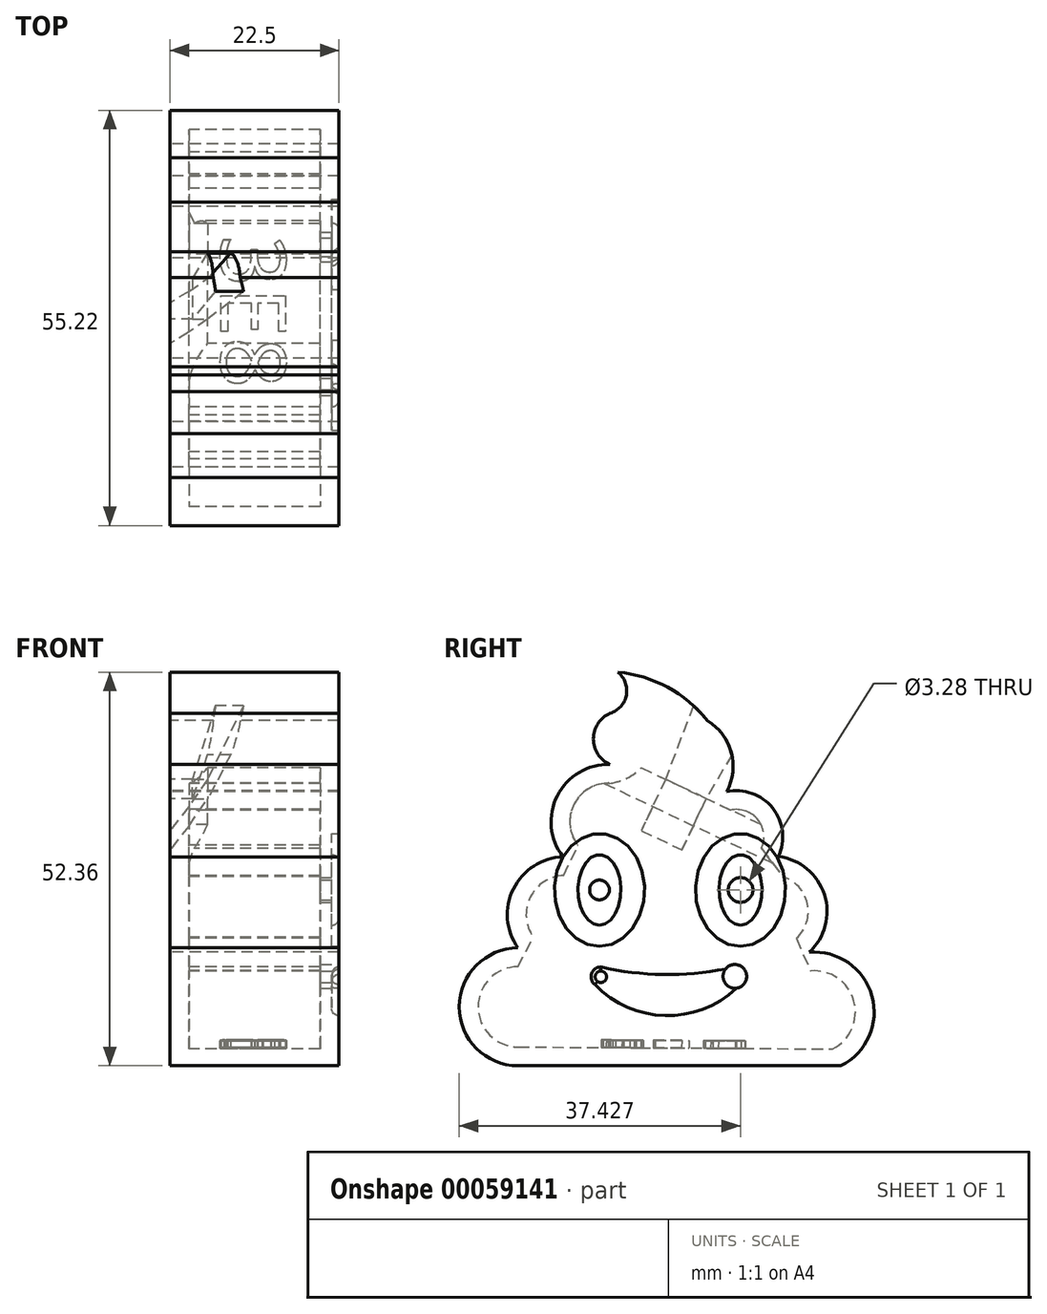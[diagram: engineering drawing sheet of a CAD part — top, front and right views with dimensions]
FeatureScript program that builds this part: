
annotation { "Feature Type Name" : "Feature", "Feature Type Description" : "" }
export const myFeature = defineFeature(function(context is Context, id is Id, definition is map)
    precondition{}
    {
        {
            var Q0;
            Q0=qCreatedBy(makeId("Top.planeOp"),FACE);
            var sketch = newSketch(context, id + "F0", { "sketchPlane" : qUnion([Q0])});
            skArc(sketch, "E0", {"start": v(-7.78, 52.75) * mm, "mid": v(-5.62, 55.18) * mm, "end": v(-6.74, 58.22) * mm});
            skArc(sketch, "E1", {"start": v(-7.78, 52.75) * mm, "mid": v(-10, 49.35) * mm, "end": v(-7.78, 45.95) * mm});
            skArc(sketch, "E2", {"start": v(-7.78, 45.95) * mm, "mid": v(-14.8, 41.8) * mm, "end": v(-14.04, 33.67) * mm});
            skArc(sketch, "E3", {"start": v(-14.04, 33.67) * mm, "mid": v(-20.65, 29.4) * mm, "end": v(-20.05, 21.54) * mm});
            skArc(sketch, "E4", {"start": v(-20.05, 21.54) * mm, "mid": v(-27.84, 13.7) * mm, "end": v(-20.05, 5.86) * mm});
            skArc(sketch, "E5", {"start": v(22.95, 5.86) * mm, "mid": v(27.07, 15.17) * mm, "end": v(18.7, 20.97) * mm});
            skArc(sketch, "E6", {"start": v(18.7, 20.97) * mm, "mid": v(20.75, 28.65) * mm, "end": v(14.63, 33.7) * mm});
            skArc(sketch, "E7", {"start": v(14.63, 33.7) * mm, "mid": v(13.85, 40.15) * mm, "end": v(7.74, 42.32) * mm});
            skArc(sketch, "E8", {"start": v(7.74, 42.32) * mm, "mid": v(8.35, 47.56) * mm, "end": v(5.18, 51.77) * mm});
            skArc(sketch, "E9", {"start": v(5.18, 51.77) * mm, "mid": v(-0.12, 56.22) * mm, "end": v(-6.74, 58.22) * mm});
            skLineSegment(sketch, "E10", {"start": v(-20.05, 5.86) * mm, "end": v(22.95, 5.86) * mm});
            skSolve(sketch);
        }
        {
            var Q0;
            Q0=makeQuery(id+"F0.imprint","IMPRINT",FACE,{"disambiguationData":[TD([[makeQuery(id+"F0.imprint","IMPRINT",EDGE,{"derivedFrom":sQuery(id+"F0.wireOp",EDGE,"E0")}),-1.0]])]});
            extrude(context, id + "F1", {"entities" : qUnion([Q0]), "depth" : 2.5 * mm});
        }
        {
            var Q0;
            Q0=makeQuery(id+"F1.opExtrude","CAP_FACE",FACE,{"disambiguationData":[OSD([sQuery(id+"F0.wireOp",EDGE,"E0"),sQuery(id+"F0.wireOp",EDGE,"E1"),sQuery(id+"F0.wireOp",EDGE,"E2"),sQuery(id+"F0.wireOp",EDGE,"E3"),sQuery(id+"F0.wireOp",EDGE,"E4"),sQuery(id+"F0.wireOp",EDGE,"E5"),sQuery(id+"F0.wireOp",EDGE,"E6"),sQuery(id+"F0.wireOp",EDGE,"E7"),sQuery(id+"F0.wireOp",EDGE,"E8"),sQuery(id+"F0.wireOp",EDGE,"E9"),sQuery(id+"F0.wireOp",EDGE,"E10")])],"isStart":false});
            var sketch = newSketch(context, id + "F2", { "sketchPlane" : qUnion([Q0])});
            skArc(sketch, "E11.0", {"start": v(-7.85, 43.45) * mm, "mid": v(-12.57, 40.66) * mm, "end": v(-12.06, 35.2) * mm});
            skArc(sketch, "E12.0", {"start": v(-13.94, 31.17) * mm, "mid": v(-18.4, 28.28) * mm, "end": v(-18, 22.98) * mm});
            skArc(sketch, "E13.0", {"start": v(-20.04, 19.04) * mm, "mid": v(-25.34, 13.7) * mm, "end": v(-20.04, 8.36) * mm});
            skArc(sketch, "E14.0", {"start": v(21.83, 8.1) * mm, "mid": v(24.67, 14.5) * mm, "end": v(18.92, 18.48) * mm});
            skArc(sketch, "E15.0", {"start": v(17.02, 22.82) * mm, "mid": v(18.48, 27.44) * mm, "end": v(15.22, 31.03) * mm});
            skArc(sketch, "E16.0", {"start": v(12.36, 34.76) * mm, "mid": v(11.9, 38.6) * mm, "end": v(8.27, 39.88) * mm});
            skLineSegment(sketch, "E17", {"start": v(-20.04, 8.36) * mm, "end": v(21.83, 8.1) * mm});
            skArc(sketch, "E18.0", {"start": v(5.18, 51.77) * mm, "mid": v(-0.12, 56.22) * mm, "end": v(-6.74, 58.22) * mm});
            skArc(sketch, "E19.0", {"start": v(7.74, 42.32) * mm, "mid": v(8.35, 47.56) * mm, "end": v(5.18, 51.77) * mm});
            skArc(sketch, "E20.0", {"start": v(14.63, 33.7) * mm, "mid": v(13.85, 40.15) * mm, "end": v(7.74, 42.32) * mm});
            skArc(sketch, "E21.0", {"start": v(18.7, 20.97) * mm, "mid": v(20.75, 28.65) * mm, "end": v(14.63, 33.7) * mm});
            skArc(sketch, "E22.0", {"start": v(22.95, 5.86) * mm, "mid": v(27.07, 15.17) * mm, "end": v(18.7, 20.97) * mm});
            skLineSegment(sketch, "E23.0", {"start": v(-20.05, 5.86) * mm, "end": v(22.95, 5.86) * mm});
            skArc(sketch, "E24.0", {"start": v(-20.05, 21.54) * mm, "mid": v(-27.84, 13.7) * mm, "end": v(-20.05, 5.86) * mm});
            skArc(sketch, "E25.0", {"start": v(-14.04, 33.67) * mm, "mid": v(-20.65, 29.4) * mm, "end": v(-20.05, 21.54) * mm});
            skArc(sketch, "E26.0", {"start": v(-7.78, 45.95) * mm, "mid": v(-14.8, 41.8) * mm, "end": v(-14.04, 33.67) * mm});
            skArc(sketch, "E27.0", {"start": v(-7.78, 52.75) * mm, "mid": v(-10, 49.35) * mm, "end": v(-7.78, 45.95) * mm});
            skArc(sketch, "E28.0", {"start": v(-7.78, 52.75) * mm, "mid": v(-5.62, 55.18) * mm, "end": v(-6.74, 58.22) * mm});
            skLineSegment(sketch, "E29", {"start": v(-20.04, 19.04) * mm, "end": v(-18, 22.98) * mm});
            skLineSegment(sketch, "E30", {"start": v(-13.94, 31.17) * mm, "end": v(-12.06, 35.2) * mm});
            skLineSegment(sketch, "E31", {"start": v(12.36, 34.76) * mm, "end": v(15.22, 31.03) * mm});
            skLineSegment(sketch, "E32", {"start": v(17.02, 22.82) * mm, "end": v(18.92, 18.48) * mm});
            skArc(sketch, "E33", {"start": v(-7.85, 43.45) * mm, "mid": v(-5.56, 44.12) * mm, "end": v(-3.62, 45.51) * mm});
            skLineSegment(sketch, "E34", {"start": v(-3.62, 45.51) * mm, "end": v(8.27, 39.88) * mm});
            skSolve(sketch);
        }
        {
            var Q0;
            Q0 = qSketchRegion(id + "F2", true);
            extrude(context, id + "F3", {"entities" : qUnion([Q0]), "operationType" : NewBodyOperationType.ADD, "depth" : 20 * mm});
        }
        {
            var Q0;
            Q0=makeQuery(id+"F3.opExtrude","SWEPT_FACE",FACE,{"disambiguationData":[OSD([sQuery(id+"F2.wireOp",EDGE,"E34")])]});
            var sketch = newSketch(context, id + "F4", { "sketchPlane" : qUnion([Q0])});
            skLineSegment(sketch, "E35.top", {"start": v(-19.19, 5) * mm, "end": v(-13.19, 5) * mm});
            skLineSegment(sketch, "E35.left", {"start": v(-19.19, 3) * mm, "end": v(-19.19, 5) * mm});
            skLineSegment(sketch, "E35.right", {"start": v(-13.19, 3) * mm, "end": v(-13.19, 5) * mm});
            skPoint(sketch, "E36", {"position": v(-16.19, 2.5) * mm});
            skLineSegment(sketch, "E37", {"start": v(-16.19, 2.5) * mm, "end": v(-16.19, 3) * mm, "construction": true});
            skLineSegment(sketch, "E38", {"start": v(-13.19, 3) * mm, "end": v(-19.19, 3) * mm});
            skSolve(sketch);
        }
        {
            var Q0;
            Q0=makeQuery(id+"F1.opExtrude","CAP_FACE",FACE,{"disambiguationData":[OSD([sQuery(id+"F0.wireOp",EDGE,"E0"),sQuery(id+"F0.wireOp",EDGE,"E1"),sQuery(id+"F0.wireOp",EDGE,"E2"),sQuery(id+"F0.wireOp",EDGE,"E3"),sQuery(id+"F0.wireOp",EDGE,"E4"),sQuery(id+"F0.wireOp",EDGE,"E5"),sQuery(id+"F0.wireOp",EDGE,"E6"),sQuery(id+"F0.wireOp",EDGE,"E7"),sQuery(id+"F0.wireOp",EDGE,"E8"),sQuery(id+"F0.wireOp",EDGE,"E9"),sQuery(id+"F0.wireOp",EDGE,"E10")])],"isStart":true});
            var sketch = newSketch(context, id + "F5", { "sketchPlane" : qUnion([Q0])});
            skLineSegment(sketch, "E39", {"start": v(-0.39, -43.98) * mm, "end": v(-1.46, -41.72) * mm});
            skLineSegment(sketch, "E40", {"start": v(-1.46, -41.72) * mm, "end": v(3.97, -39.15) * mm});
            skLineSegment(sketch, "E41", {"start": v(3.97, -39.15) * mm, "end": v(5.04, -41.4) * mm});
            skLineSegment(sketch, "E42", {"start": v(5.04, -41.4) * mm, "end": v(-0.39, -43.98) * mm});
            skPoint(sketch, "E43", {"position": v(2.33, -42.7) * mm});
            skPoint(sketch, "E44.0", {"position": v(-3.62, -45.51) * mm});
            skPoint(sketch, "E45.0", {"position": v(8.27, -39.88) * mm});
            skLineSegment(sketch, "E46", {"start": v(-3.62, -45.51) * mm, "end": v(8.27, -39.88) * mm, "construction": true});
            skSolve(sketch);
        }
        {
            var Q0;
            Q0=makeQuery(id+"F3.opExtrude","CAP_FACE",FACE,{"disambiguationData":[OSD([sQuery(id+"F2.wireOp",EDGE,"E11.0"),sQuery(id+"F2.wireOp",EDGE,"E12.0"),sQuery(id+"F2.wireOp",EDGE,"E13.0"),sQuery(id+"F2.wireOp",EDGE,"E14.0"),sQuery(id+"F2.wireOp",EDGE,"E15.0"),sQuery(id+"F2.wireOp",EDGE,"E16.0"),sQuery(id+"F2.wireOp",EDGE,"E17"),sQuery(id+"F2.wireOp",EDGE,"E18.0"),sQuery(id+"F2.wireOp",EDGE,"E19.0"),sQuery(id+"F2.wireOp",EDGE,"E20.0"),sQuery(id+"F2.wireOp",EDGE,"E21.0"),sQuery(id+"F2.wireOp",EDGE,"E22.0"),sQuery(id+"F2.wireOp",EDGE,"E23.0"),sQuery(id+"F2.wireOp",EDGE,"E24.0"),sQuery(id+"F2.wireOp",EDGE,"E25.0"),sQuery(id+"F2.wireOp",EDGE,"E26.0"),sQuery(id+"F2.wireOp",EDGE,"E27.0"),sQuery(id+"F2.wireOp",EDGE,"E28.0"),sQuery(id+"F2.wireOp",EDGE,"E29"),sQuery(id+"F2.wireOp",EDGE,"E30"),sQuery(id+"F2.wireOp",EDGE,"E31"),sQuery(id+"F2.wireOp",EDGE,"E32"),sQuery(id+"F2.wireOp",EDGE,"E33"),sQuery(id+"F2.wireOp",EDGE,"E34")])],"isStart":false});
            var sketch = newSketch(context, id + "F6", { "sketchPlane" : qUnion([Q0])});
            skLineSegment(sketch, "E47.0", {"start": v(-3.62, 45.51) * mm, "end": v(8.27, 39.88) * mm});
            skArc(sketch, "E48.0", {"start": v(-7.85, 43.45) * mm, "mid": v(-5.56, 44.12) * mm, "end": v(-3.62, 45.51) * mm});
            skArc(sketch, "E49.0", {"start": v(-7.85, 43.45) * mm, "mid": v(-12.57, 40.66) * mm, "end": v(-12.06, 35.2) * mm});
            skLineSegment(sketch, "E50.0", {"start": v(-13.94, 31.17) * mm, "end": v(-12.06, 35.2) * mm});
            skArc(sketch, "E51.0", {"start": v(-13.94, 31.17) * mm, "mid": v(-18.4, 28.28) * mm, "end": v(-18, 22.98) * mm});
            skLineSegment(sketch, "E52.0", {"start": v(-20.04, 19.04) * mm, "end": v(-18, 22.98) * mm});
            skArc(sketch, "E53.0", {"start": v(-20.04, 19.04) * mm, "mid": v(-25.34, 13.7) * mm, "end": v(-20.04, 8.36) * mm});
            skLineSegment(sketch, "E54.0", {"start": v(-20.04, 8.36) * mm, "end": v(21.83, 8.1) * mm});
            skArc(sketch, "E55.0", {"start": v(21.83, 8.1) * mm, "mid": v(24.67, 14.5) * mm, "end": v(18.92, 18.48) * mm});
            skLineSegment(sketch, "E56.0", {"start": v(17.02, 22.82) * mm, "end": v(18.92, 18.48) * mm});
            skArc(sketch, "E57.0", {"start": v(17.02, 22.82) * mm, "mid": v(18.48, 27.44) * mm, "end": v(15.22, 31.03) * mm});
            skLineSegment(sketch, "E58.0", {"start": v(12.36, 34.76) * mm, "end": v(15.22, 31.03) * mm});
            skArc(sketch, "E59.0", {"start": v(12.36, 34.76) * mm, "mid": v(11.9, 38.6) * mm, "end": v(8.27, 39.88) * mm});
            skSolve(sketch);
        }
        {
            var Q0;
            Q0=makeQuery(id+"F6.imprint","IMPRINT",FACE,{"disambiguationData":[TD([[makeQuery(id+"F6.imprint","IMPRINT",EDGE,{"derivedFrom":sQuery(id+"F6.wireOp",EDGE,"E47.0")}),-1.0]])]});
            extrude(context, id + "F7", {"entities" : qUnion([Q0]), "operationType" : NewBodyOperationType.ADD, "oppositeDirection" : true, "depth" : 2.5 * mm});
        }
        {
            var Q0;
            Q0=makeQuery(id+"F7.boolean.opBoolean","MERGE",FACE,{"derivedFrom":[makeQuery(id+"F3.opExtrude","CAP_FACE",FACE,{"disambiguationData":[OSD([sQuery(id+"F2.wireOp",EDGE,"E11.0"),sQuery(id+"F2.wireOp",EDGE,"E12.0"),sQuery(id+"F2.wireOp",EDGE,"E13.0"),sQuery(id+"F2.wireOp",EDGE,"E14.0"),sQuery(id+"F2.wireOp",EDGE,"E15.0"),sQuery(id+"F2.wireOp",EDGE,"E16.0"),sQuery(id+"F2.wireOp",EDGE,"E17"),sQuery(id+"F2.wireOp",EDGE,"E18.0"),sQuery(id+"F2.wireOp",EDGE,"E19.0"),sQuery(id+"F2.wireOp",EDGE,"E20.0"),sQuery(id+"F2.wireOp",EDGE,"E21.0"),sQuery(id+"F2.wireOp",EDGE,"E22.0"),sQuery(id+"F2.wireOp",EDGE,"E23.0"),sQuery(id+"F2.wireOp",EDGE,"E24.0"),sQuery(id+"F2.wireOp",EDGE,"E25.0"),sQuery(id+"F2.wireOp",EDGE,"E26.0"),sQuery(id+"F2.wireOp",EDGE,"E27.0"),sQuery(id+"F2.wireOp",EDGE,"E28.0"),sQuery(id+"F2.wireOp",EDGE,"E29"),sQuery(id+"F2.wireOp",EDGE,"E30"),sQuery(id+"F2.wireOp",EDGE,"E31"),sQuery(id+"F2.wireOp",EDGE,"E32"),sQuery(id+"F2.wireOp",EDGE,"E33"),sQuery(id+"F2.wireOp",EDGE,"E34")])],"isStart":false}),makeQuery(id+"F7.opExtrude","CAP_FACE",FACE,{"disambiguationData":[OSD([sQuery(id+"F6.wireOp",EDGE,"E47.0"),sQuery(id+"F6.wireOp",EDGE,"E48.0"),sQuery(id+"F6.wireOp",EDGE,"E49.0"),sQuery(id+"F6.wireOp",EDGE,"E50.0"),sQuery(id+"F6.wireOp",EDGE,"E51.0"),sQuery(id+"F6.wireOp",EDGE,"E52.0"),sQuery(id+"F6.wireOp",EDGE,"E53.0"),sQuery(id+"F6.wireOp",EDGE,"E54.0"),sQuery(id+"F6.wireOp",EDGE,"E55.0"),sQuery(id+"F6.wireOp",EDGE,"E56.0"),sQuery(id+"F6.wireOp",EDGE,"E57.0"),sQuery(id+"F6.wireOp",EDGE,"E58.0"),sQuery(id+"F6.wireOp",EDGE,"E59.0")])],"isStart":true})]});
            var sketch = newSketch(context, id + "F8", { "sketchPlane" : qUnion([Q0])});
            skLineSegment(sketch, "E60", {"start": v(1.45, 5.86) * mm, "end": v(0.2, 5.86) * mm, "construction": true});
            skLineSegment(sketch, "E61", {"start": v(0.2, 5.86) * mm, "end": v(0.2, 39.46) * mm, "construction": true});
            skLineSegment(sketch, "E62", {"start": v(0.2, 29.25) * mm, "end": v(-9.18, 29.25) * mm, "construction": true});
            skEllipse(sketch, "E63", {"center": v(-9.18, 29.25) * mm, "majorRadius": 7.5 * mm, "minorRadius": 6 * mm, "majorAxis": v(0, -1)});
            skEllipse(sketch, "E64.MirrorC", {"center": v(9.58, 29.25) * mm, "majorRadius": 7.5 * mm, "minorRadius": 6 * mm, "majorAxis": v(0, -1)});
            skArc(sketch, "E65", {"start": v(-9, 19) * mm, "mid": v(-0.09, 18) * mm, "end": v(8.83, 19) * mm});
            skLineSegment(sketch, "E66", {"start": v(-9, 19) * mm, "end": v(8.83, 19) * mm, "construction": true});
            skArc(sketch, "E67", {"start": v(-9.79, 16.67) * mm, "mid": v(0.02, 12.54) * mm, "end": v(9.73, 16.9) * mm});
            skArc(sketch, "E68", {"start": v(-9, 19) * mm, "mid": v(-10.24, 18.12) * mm, "end": v(-9.79, 16.67) * mm});
            skArc(sketch, "E69", {"start": v(9.73, 16.9) * mm, "mid": v(9.97, 18.25) * mm, "end": v(8.83, 19) * mm});
            skSolve(sketch);
        }
        {
            var Q0;
            Q0 = qSketchRegion(id + "F8", true);
            extrude(context, id + "F9", {"entities" : qUnion([Q0]), "operationType" : NewBodyOperationType.REMOVE, "oppositeDirection" : true, "depth" : 1 * mm});
        }
        {
            var Q0;
            Q0=makeQuery(id+"F9.boolean.opBoolean","COPY",FACE,{"derivedFrom":makeQuery(id+"F9.opExtrude","CAP_FACE",FACE,{"disambiguationData":[OSD([sQuery(id+"F8.wireOp",EDGE,"E63")])],"isStart":false})});
            var sketch = newSketch(context, id + "F10", { "sketchPlane" : qUnion([Q0])});
            skPoint(sketch, "E70.0", {"position": v(-9.18, 29.25) * mm});
            skLineSegment(sketch, "E71.0", {"start": v(0.2, 5.86) * mm, "end": v(0.2, 39.46) * mm, "construction": true});
            skEllipse(sketch, "E72", {"center": v(-9.18, 29.25) * mm, "majorRadius": 4.69 * mm, "minorRadius": 2.86 * mm, "majorAxis": v(0, -1)});
            skEllipse(sketch, "E73.MirrorC", {"center": v(9.58, 29.25) * mm, "majorRadius": 4.69 * mm, "minorRadius": 2.86 * mm, "majorAxis": v(0, -1)});
            skSolve(sketch);
        }
        {
            var Q0;
            Q0 = qSketchRegion(id + "F10", true);
            extrude(context, id + "F11", {"entities" : qUnion([Q0]), "operationType" : NewBodyOperationType.ADD, "depth" : 1 * mm});
        }
        {
            var Q0;
            Q0=makeQuery(id+"F11.opExtrude","CAP_EDGE",EDGE,{"disambiguationData":[OSD([sQuery(id+"F10.wireOp",EDGE,"E72")])],"isStart":false});
            var Q1;
            Q1=makeQuery(id+"F11.opExtrude","CAP_EDGE",EDGE,{"disambiguationData":[OSD([sQuery(id+"F10.wireOp",EDGE,"E73.MirrorC")])],"isStart":false});
            var Q2;
            Q2=makeQuery(id+"F9.boolean.opBoolean","COPY",FACE,{"derivedFrom":makeQuery(id+"F9.opExtrude","CAP_FACE",FACE,{"disambiguationData":[OSD([sQuery(id+"F8.wireOp",EDGE,"E65"),sQuery(id+"F8.wireOp",EDGE,"E67"),sQuery(id+"F8.wireOp",EDGE,"E68"),sQuery(id+"F8.wireOp",EDGE,"E69")])],"isStart":false})});
            fillet(context, id + "F12", {"entities" : qUnion([Q0, Q1, Q2]), "radius" : 1 * mm, "tangentPropagation" : true, "allowEdgeOverflow" : false});
        }
        {
            var Q0;
            Q0=makeQuery(id+"F8.imprint","IMPRINT",FACE,{"disambiguationData":[TD([[makeQuery(id+"F8.imprint","IMPRINT",EDGE,{"derivedFrom":sQuery(id+"F8.wireOp",EDGE,"E63")}),-1.0]])]});
            cPlane(context, id + "F13", {"entities" : qUnion([Q0]), "cplaneType" : CPlaneType.OFFSET, "offset" : 1 * mm, "width" : 150 * mm, "height" : 150 * mm});
        }
        {
            var Q0;
            Q0=qCreatedBy(id+"F13.planeOp",FACE);
            var sketch = newSketch(context, id + "F14", { "sketchPlane" : qUnion([Q0])});
            skPoint(sketch, "E74.0", {"position": v(-9.18, 29.25) * mm});
            skPoint(sketch, "E75.0", {"position": v(9.58, 29.25) * mm});
            skPoint(sketch, "E76.0", {"position": v(-9, 17.7) * mm});
            skPoint(sketch, "E77.0", {"position": v(8.83, 17.76) * mm});
            skCircle(sketch, "E78", {"center": v(-9.18, 29.25) * mm, "radius": 1.31 * mm});
            skCircle(sketch, "E79", {"center": v(9.58, 29.25) * mm, "radius": 1.64 * mm});
            skCircle(sketch, "E80", {"center": v(-9, 17.7) * mm, "radius": 0.76 * mm});
            skCircle(sketch, "E81", {"center": v(8.83, 17.76) * mm, "radius": 1.57 * mm});
            skSolve(sketch);
        }
        {
            var Q0;
            Q0 = qSketchRegion(id + "F14", true);
            extrude(context, id + "F15", {"entities" : qUnion([Q0]), "operationType" : NewBodyOperationType.REMOVE, "oppositeDirection" : true, "depth" : 10 * mm});
        }
        {
            var Q0;
            Q0=makeQuery(id+"F3.opExtrude","SWEPT_FACE",FACE,{"disambiguationData":[OSD([sQuery(id+"F2.wireOp",EDGE,"E17")])]});
            var sketch = newSketch(context, id + "F16", { "sketchPlane" : qUnion([Q0])});
            skText(sketch, "E82", { "text": "3E8", "fontName": "OpenSans-Regular.ttf"});
            const initialGuessF16  = {"E82": [-0.0107, 0.0068, 1, 0, 0.00861]};
            skSetInitialGuess(sketch, initialGuessF16);
            skSolve(sketch);
        }
        {
            var Q0;
            Q0 = qSketchRegion(id + "F16", true);
            extrude(context, id + "F17", {"entities" : qUnion([Q0]), "operationType" : NewBodyOperationType.ADD, "depth" : 1 * mm});
        }
        {
            var Q0;
            Q0=makeQuery(id+"F21.boolean.opBoolean","MERGE",FACE,{"derivedFrom":[makeQuery(id+"F3.opExtrude","SWEPT_FACE",FACE,{"disambiguationData":[OSD([sQuery(id+"F2.wireOp",EDGE,"E34")])]}),makeQuery(id+"F21.opExtrude","SWEPT_FACE",FACE,{"disambiguationData":[OSD([sQuery(id+"F5.wireOp",EDGE,"E42")])]})]});
            cPlane(context, id + "F18", {"entities" : qUnion([Q0]), "cplaneType" : CPlaneType.OFFSET, "offset" : 12 * mm, "oppositeDirection" : true, "width" : 150 * mm, "height" : 150 * mm});
        }
        {
            var Q0;
            Q0=qCreatedBy(id+"F18.planeOp",FACE);
            var sketch = newSketch(context, id + "F19", { "sketchPlane" : qUnion([Q0])});
            skLineSegment(sketch, "E83.0.1", {"start": v(-19.19, 0) * mm, "end": v(-13.19, 0) * mm, "construction": true});
            skLineSegment(sketch, "E84.0", {"start": v(-13.19, 3) * mm, "end": v(-19.19, 3) * mm, "construction": true});
            skLineSegment(sketch, "E85.0", {"start": v(-13.19, 3) * mm, "end": v(-13.19, 5) * mm, "construction": true});
            skLineSegment(sketch, "E86.0", {"start": v(-19.19, 5) * mm, "end": v(-13.19, 5) * mm, "construction": true});
            skLineSegment(sketch, "E87.0", {"start": v(-19.19, 3) * mm, "end": v(-19.19, 5) * mm, "construction": true});
            skLineSegment(sketch, "E88.0", {"start": v(-17.5, 22.5) * mm, "end": v(-11.13, 22.5) * mm, "construction": true});
            skPoint(sketch, "E89.endSnap0", {"position": v(-16.19, 5) * mm});
            skLineSegment(sketch, "E90.rect.bottom", {"start": v(-20.19, 10.5) * mm, "end": v(-12.19, 10.5) * mm});
            skLineSegment(sketch, "E90.rect.top", {"start": v(-20.19, 6.5) * mm, "end": v(-12.19, 6.5) * mm});
            skLineSegment(sketch, "E90.rect.left", {"start": v(-20.19, 10.5) * mm, "end": v(-20.19, 6.5) * mm});
            skLineSegment(sketch, "E90.rect.right", {"start": v(-12.19, 10.5) * mm, "end": v(-12.19, 6.5) * mm});
            skPoint(sketch, "E90.rect.middle", {"position": v(-16.19, 8.5) * mm});
            skLineSegment(sketch, "E91", {"start": v(-16.19, 10.5) * mm, "end": v(-16.19, 22.5) * mm, "construction": true});
            skSolve(sketch);
        }
        {
            var Q1;
            Q1=makeQuery(id+"F19.imprint","IMPRINT",FACE,{"disambiguationData":[TD([[makeQuery(id+"F19.imprint","IMPRINT",EDGE,{"derivedFrom":sQuery(id+"F19.wireOp",EDGE,"E90.rect.bottom")}),-1.0]])]});
            var Q2;
            Q2 = qSketchRegion(id + "F4", true);
            loft(context, id + "F20", {"operationType" : NewBodyOperationType.REMOVE, "sheetProfilesArray" : [{ "sheetProfileEntities" : qUnion([Q1]) }, { "sheetProfileEntities" : qUnion([Q2]) }]});
        }
        {
            var Q0;
            Q0 = qSketchRegion(id + "F5", true);
            extrude(context, id + "F21", {"entities" : qUnion([Q0]), "operationType" : NewBodyOperationType.REMOVE, "oppositeDirection" : true, "depth" : 2.5 * mm});
        }
        {
            var Q0;
            Q0=makeQuery(id+"F21.boolean.opBoolean","COPY",FACE,{"derivedFrom":makeQuery(id+"F21.opExtrude","SWEPT_FACE",FACE,{"disambiguationData":[OSD([sQuery(id+"F5.wireOp",EDGE,"E41")])]})});
            var sketch = newSketch(context, id + "F22", { "sketchPlane" : qUnion([Q0])});
            skLineSegment(sketch, "E92.0.0", {"start": v(-39.58, 0) * mm, "end": v(-37.08, 0) * mm, "construction": true});
            skLineSegment(sketch, "E92.0.1", {"start": v(-37.08, 0) * mm, "end": v(-37.08, 2.5) * mm, "construction": true});
            skLineSegment(sketch, "E92.0.2", {"start": v(-37.08, 2.5) * mm, "end": v(-39.58, 2.5) * mm, "construction": true});
            skLineSegment(sketch, "E92.0.3", {"start": v(-39.58, 2.5) * mm, "end": v(-39.58, 0) * mm, "construction": true});
            skLineSegment(sketch, "E93.0.0", {"start": v(-46.3, 4.96) * mm, "end": v(-39.58, 3) * mm, "construction": true});
            skLineSegment(sketch, "E93.0.1", {"start": v(-39.58, 3) * mm, "end": v(-39.58, 5) * mm, "construction": true});
            skLineSegment(sketch, "E93.0.2", {"start": v(-39.58, 5) * mm, "end": v(-46.3, 8.08) * mm, "construction": true});
            skLineSegment(sketch, "E93.0.3", {"start": v(-46.3, 4.96) * mm, "end": v(-46.3, 8.08) * mm, "construction": true});
            skLineSegment(sketch, "E94", {"start": v(-46.3, 6.52) * mm, "end": v(-39.58, 4) * mm, "construction": true});
            skLineSegment(sketch, "E95", {"start": v(-39.58, 4) * mm, "end": v(-28.57, -0.13) * mm, "construction": true});
            skLineSegment(sketch, "E96.0.0", {"start": v(-49.72, 0) * mm, "end": v(-44.34, 0) * mm, "construction": true});
            skLineSegment(sketch, "E96.0.1", {"start": v(-49, 0) * mm, "end": v(-50.78, 0) * mm, "construction": true});
            skLineSegment(sketch, "E96.0.2", {"start": v(-41.56, 0) * mm, "end": v(-49, 0) * mm, "construction": true});
            skLineSegment(sketch, "E96.0.3", {"start": v(-36.72, 0) * mm, "end": v(-42.84, 0) * mm, "construction": true});
            skLineSegment(sketch, "E96.0.4", {"start": v(-26.96, 0) * mm, "end": v(-37.1, 0) * mm, "construction": true});
            skLineSegment(sketch, "E96.0.5", {"start": v(-15.13, 0) * mm, "end": v(-28.05, 0) * mm, "construction": true});
            skLineSegment(sketch, "E96.0.6", {"start": v(-15.13, 0) * mm, "end": v(3.29, 0) * mm, "construction": true});
            skLineSegment(sketch, "E96.0.7", {"start": v(4.02, 0) * mm, "end": v(-10.88, 0) * mm, "construction": true});
            skLineSegment(sketch, "E96.0.8", {"start": v(-10.88, 0) * mm, "end": v(-24.41, 0) * mm, "construction": true});
            skLineSegment(sketch, "E96.0.9", {"start": v(-24.41, 0) * mm, "end": v(-38.19, 0) * mm, "construction": true});
            skLineSegment(sketch, "E96.0.10", {"start": v(-38.19, 0) * mm, "end": v(-44.34, 0) * mm, "construction": true});
            skLineSegment(sketch, "E97.0.2", {"start": v(-35.9, 2.5) * mm, "end": v(-39.58, 2.5) * mm, "construction": true});
            skLineSegment(sketch, "E97.0.3", {"start": v(-35.9, 2.5) * mm, "end": v(-26.64, 2.5) * mm, "construction": true});
            skLineSegment(sketch, "E97.0.4", {"start": v(-26.64, 2.5) * mm, "end": v(-22.2, 2.5) * mm, "construction": true});
            skLineSegment(sketch, "E97.0.5", {"start": v(-22.2, 2.5) * mm, "end": v(-13.05, 2.5) * mm, "construction": true});
            skLineSegment(sketch, "E97.0.6", {"start": v(-13.05, 2.5) * mm, "end": v(-8.63, 2.5) * mm, "construction": true});
            skLineSegment(sketch, "E97.0.7", {"start": v(-8.63, 2.5) * mm, "end": v(1.52, 2.5) * mm, "construction": true});
            skLineSegment(sketch, "E97.0.8", {"start": v(1.02, 2.5) * mm, "end": v(-16.67, 2.5) * mm, "construction": true});
            skLineSegment(sketch, "E97.0.9", {"start": v(-25.55, 2.5) * mm, "end": v(-16.67, 2.5) * mm, "construction": true});
            skLineSegment(sketch, "E97.0.10", {"start": v(-24.8, 2.5) * mm, "end": v(-27.9, 2.5) * mm, "construction": true});
            skLineSegment(sketch, "E97.0.11", {"start": v(-34.6, 2.5) * mm, "end": v(-27.9, 2.5) * mm, "construction": true});
            skLineSegment(sketch, "E97.0.12", {"start": v(-34.56, 2.5) * mm, "end": v(-36.7, 2.5) * mm, "construction": true});
            skLineSegment(sketch, "E97.0.13", {"start": v(-40.34, 2.5) * mm, "end": v(-36.7, 2.5) * mm, "construction": true});
            skLineSegment(sketch, "E97.0.15", {"start": v(-39.58, 2.5) * mm, "end": v(-37.08, 2.5) * mm, "construction": true});
            skLineSegment(sketch, "E98", {"start": v(-35.58, 2.5) * mm, "end": v(-28.9, 0) * mm, "construction": true});
            skLineSegment(sketch, "E99", {"start": v(-28.9, 0) * mm, "end": v(-37.08, 0) * mm});
            skLineSegment(sketch, "E100", {"start": v(-37.08, 2.5) * mm, "end": v(-35.58, 2.5) * mm});
            skLineSegment(sketch, "E101", {"start": v(-35.58, 2.5) * mm, "end": v(-32.03, 0) * mm});
            skLineSegment(sketch, "E102", {"start": v(-32.03, 0) * mm, "end": v(-28.57, -0.13) * mm});
            skSolve(sketch);
        }
        {
            var Q0;
            Q0=makeQuery(id+"F22.imprint","IMPRINT",FACE,{"disambiguationData":[TD([[makeQuery(id+"F22.imprint","IMPRINT",EDGE,{"derivedFrom":sQuery(id+"F22.wireOp",EDGE,"E100")}),-1.0]])]});
            extrude(context, id + "F23", {"entities" : qUnion([Q0]), "operationType" : NewBodyOperationType.REMOVE, "depth" : 6 * mm});
        }
        {
            var Q0;
            Q0=makeQuery(id+"F1.opExtrude","SWEPT_BODY",BODY,{"disambiguationData":[OSD([sQuery(id+"F0.wireOp",EDGE,"E0"),sQuery(id+"F0.wireOp",EDGE,"E1"),sQuery(id+"F0.wireOp",EDGE,"E2"),sQuery(id+"F0.wireOp",EDGE,"E3"),sQuery(id+"F0.wireOp",EDGE,"E4"),sQuery(id+"F0.wireOp",EDGE,"E5"),sQuery(id+"F0.wireOp",EDGE,"E6"),sQuery(id+"F0.wireOp",EDGE,"E7"),sQuery(id+"F0.wireOp",EDGE,"E8"),sQuery(id+"F0.wireOp",EDGE,"E9"),sQuery(id+"F0.wireOp",EDGE,"E10")])]});
            var Q1;
            Q1=makeQuery(id+"F1.opExtrude","CAP_EDGE",EDGE,{"disambiguationData":[OSD([sQuery(id+"F0.wireOp",EDGE,"E10")])],"isStart":true});
            transform(context, id + "F24", {"entities" : qUnion([Q0]), "transformType" : TransformType.ROTATION, "transformAxis" : qUnion([Q1]), "angle" : 90 * degree, "makeCopy" : false});
        }
        {
            var Q0;
            Q0=makeQuery(id+"F1.opExtrude","CAP_FACE",FACE,{"disambiguationData":[OSD([sQuery(id+"F0.wireOp",EDGE,"E0"),sQuery(id+"F0.wireOp",EDGE,"E1"),sQuery(id+"F0.wireOp",EDGE,"E2"),sQuery(id+"F0.wireOp",EDGE,"E3"),sQuery(id+"F0.wireOp",EDGE,"E4"),sQuery(id+"F0.wireOp",EDGE,"E5"),sQuery(id+"F0.wireOp",EDGE,"E6"),sQuery(id+"F0.wireOp",EDGE,"E7"),sQuery(id+"F0.wireOp",EDGE,"E8"),sQuery(id+"F0.wireOp",EDGE,"E9"),sQuery(id+"F0.wireOp",EDGE,"E10")])],"isStart":true});
            var sketch = newSketch(context, id + "F25", { "sketchPlane" : qUnion([Q0])});
            skLineSegment(sketch, "E103", {"start": v(0, 22.64) * mm, "end": v(0, 1.83) * mm, "construction": true});
            skSolve(sketch);
        }
        {
            var Q0;
            Q0=makeQuery(id+"F1.opExtrude","SWEPT_BODY",BODY,{"disambiguationData":[OSD([sQuery(id+"F0.wireOp",EDGE,"E0"),sQuery(id+"F0.wireOp",EDGE,"E1"),sQuery(id+"F0.wireOp",EDGE,"E2"),sQuery(id+"F0.wireOp",EDGE,"E3"),sQuery(id+"F0.wireOp",EDGE,"E4"),sQuery(id+"F0.wireOp",EDGE,"E5"),sQuery(id+"F0.wireOp",EDGE,"E6"),sQuery(id+"F0.wireOp",EDGE,"E7"),sQuery(id+"F0.wireOp",EDGE,"E8"),sQuery(id+"F0.wireOp",EDGE,"E9"),sQuery(id+"F0.wireOp",EDGE,"E10")])]});
            var Q1;
            Q1=sQuery(id+"F25.wireOp",EDGE,"E103");
            transform(context, id + "F26", {"entities" : qUnion([Q0]), "transformType" : TransformType.ROTATION, "transformAxis" : qUnion([Q1]), "angle" : 90 * degree, "oppositeDirection" : true, "makeCopy" : false});
        }
        {
            var Q0;
            Q0=makeQuery(id+"F1.opExtrude","SWEPT_BODY",BODY,{"disambiguationData":[OSD([sQuery(id+"F0.wireOp",EDGE,"E0"),sQuery(id+"F0.wireOp",EDGE,"E1"),sQuery(id+"F0.wireOp",EDGE,"E2"),sQuery(id+"F0.wireOp",EDGE,"E3"),sQuery(id+"F0.wireOp",EDGE,"E4"),sQuery(id+"F0.wireOp",EDGE,"E5"),sQuery(id+"F0.wireOp",EDGE,"E6"),sQuery(id+"F0.wireOp",EDGE,"E7"),sQuery(id+"F0.wireOp",EDGE,"E8"),sQuery(id+"F0.wireOp",EDGE,"E9"),sQuery(id+"F0.wireOp",EDGE,"E10")])]});
            transform(context, id + "F27", {"entities" : qUnion([Q0]), "transformType" : TransformType.TRANSLATION_3D, "dx" : 0 * mm, "dy" : 25 * mm, "dz" : 0 * mm, "makeCopy" : false});
        }
        {
            var Q0;
            Q0=makeQuery(id+"F23.boolean.opBoolean","MERGE",FACE,{"derivedFrom":[makeQuery(id+"F21.boolean.opBoolean","COPY",FACE,{"derivedFrom":makeQuery(id+"F21.opExtrude","SWEPT_FACE",FACE,{"disambiguationData":[OSD([sQuery(id+"F5.wireOp",EDGE,"E39")])]})}),makeQuery(id+"F23.opExtrude","CAP_FACE",FACE,{"disambiguationData":[OSD([sQuery(id+"F5.wireOp",EDGE,"E40"),sQuery(id+"F5.wireOp",EDGE,"E41"),sQuery(id+"F22.wireOp",EDGE,"E99"),sQuery(id+"F22.wireOp",EDGE,"E100"),sQuery(id+"F22.wireOp",EDGE,"E101")])],"isStart":false})]});
            var sketch = newSketch(context, id + "F28", { "sketchPlane" : qUnion([Q0])});
            skPoint(sketch, "E104.0", {"position": v(-2.5, 47.5) * mm});
            skPoint(sketch, "E105.0", {"position": v(-5, 47.5) * mm});
            skPoint(sketch, "E106.0", {"position": v(-2.5, 43.5) * mm});
            skLineSegment(sketch, "E107", {"start": v(-2.5, 47.5) * mm, "end": v(-5, 47.5) * mm});
            skLineSegment(sketch, "E108", {"start": v(-2.5, 43.5) * mm, "end": v(-2.5, 47.5) * mm});
            skLineSegment(sketch, "E109", {"start": v(-5, 47.5) * mm, "end": v(-2.5, 43.5) * mm});
            skSolve(sketch);
        }
        {
            var Q0;
            Q0 = qSketchRegion(id + "F28", true);
            extrude(context, id + "F29", {"entities" : qUnion([Q0]), "operationType" : NewBodyOperationType.ADD, "endBound" : BoundingType.UP_TO_NEXT, "oppositeDirection" : true, "depth" : 25 * mm});
        }
        {
            var Q0;
            {var subQ0=sQuery(id+"F5.wireOp",EDGE,"E41");Q0=makeQuery(id+"F23.boolean.opBoolean","MERGE",FACE,{"derivedFrom":[makeQuery(id+"F21.boolean.opBoolean","COPY",FACE,{"derivedFrom":makeQuery(id+"F21.opExtrude","SWEPT_FACE",FACE,{"disambiguationData":[OSD([subQ0])]})}),makeQuery(id+"F23.opExtrude","CAP_FACE",FACE,{"disambiguationData":[OSD([sQuery(id+"F5.wireOp",EDGE,"E40"),subQ0,sQuery(id+"F22.wireOp",EDGE,"E99"),sQuery(id+"F22.wireOp",EDGE,"E100"),sQuery(id+"F22.wireOp",EDGE,"E101")])],"isStart":true})]});}
            var sketch = newSketch(context, id + "F30", { "sketchPlane" : qUnion([Q0])});
            skPoint(sketch, "E110.0", {"position": v(2.5, 47.5) * mm});
            skPoint(sketch, "E111.0", {"position": v(5, 47.5) * mm});
            skPoint(sketch, "E112.0", {"position": v(2.5, 43.5) * mm});
            skLineSegment(sketch, "E113", {"start": v(5, 47.5) * mm, "end": v(2.5, 47.5) * mm});
            skLineSegment(sketch, "E114", {"start": v(2.5, 47.5) * mm, "end": v(2.5, 43.5) * mm});
            skLineSegment(sketch, "E115", {"start": v(2.5, 43.5) * mm, "end": v(5, 47.5) * mm});
            skSolve(sketch);
        }
        {
            var Q0;
            Q0 = qSketchRegion(id + "F30", true);
            extrude(context, id + "F31", {"entities" : qUnion([Q0]), "operationType" : NewBodyOperationType.ADD, "endBound" : BoundingType.UP_TO_NEXT, "oppositeDirection" : true, "depth" : 25 * mm});
        }
    });
